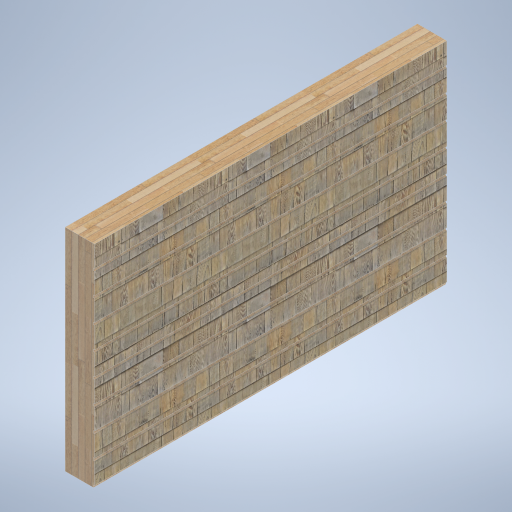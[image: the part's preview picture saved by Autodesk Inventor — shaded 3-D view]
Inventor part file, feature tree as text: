
AUTODESK INVENTOR PART (.ipt)
format: ipt  version: 2024.2 (Build 282272000, 272)  size: 532,992 bytes
history: native  units: mm
features: extrude x2, sketch x2
ambient origin geometry x8: Origin, YZ Plane, XZ Plane, XY Plane, X Axis, Y Axis, Z Axis, Center Point
bodies: Solid1 (feature_tree)
feature tree (4):
  extrude  "Extrusion1"  Depth=180.0mm
  extrude  "Extrusion2"  Depth=180.0mm
  sketch  "Sketch1"  dims[d0=250.0mm d1=0.0mm d2=180.0mm]
  sketch  "Sketch2"  dims[d3=20.0mm d4=180.0mm d5=180.0mm d6=180.0mm d7=180.0mm d8=180.0mm d9=180.0mm d10=180.0mm d11=0.0mm d12=0.0mm]
